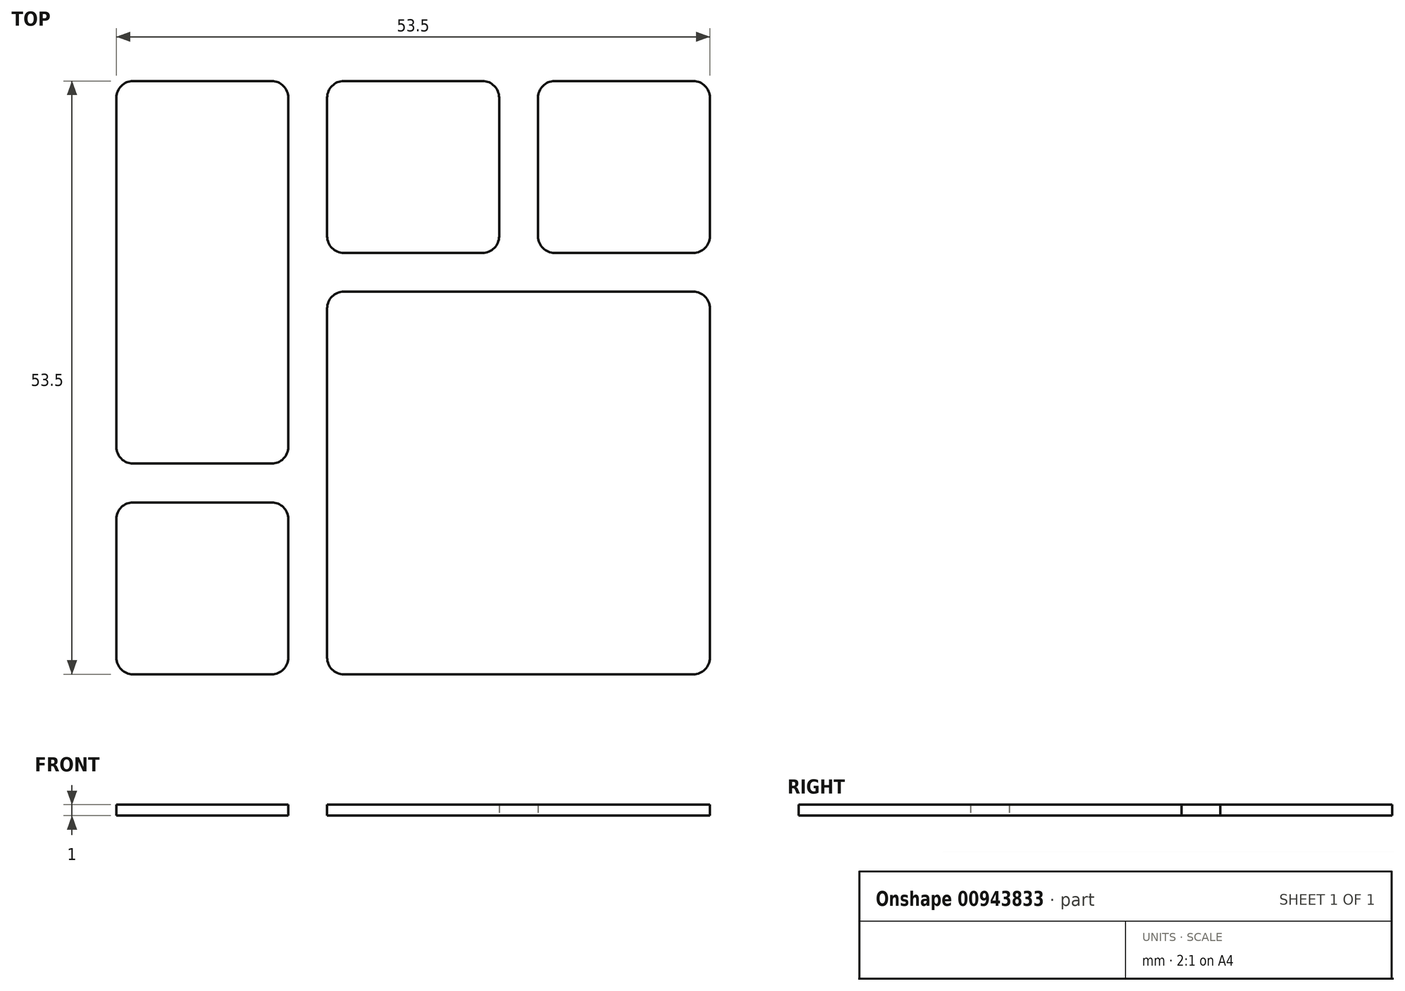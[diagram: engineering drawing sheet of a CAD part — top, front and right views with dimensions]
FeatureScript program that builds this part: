
annotation { "Feature Type Name" : "Feature", "Feature Type Description" : "" }
export const myFeature = defineFeature(function(context is Context, id is Id, definition is map)
    precondition{}
    {
        {
            var Q0;
            Q0=qCreatedBy(makeId("Top.planeOp"),FACE);
            var sketch = newSketch(context, id + "F0", { "sketchPlane" : qUnion([Q0])});
            skLineSegment(sketch, "E0.bottom", {"start": v(28.5, 28.5) * mm, "end": v(-28.5, 28.5) * mm, "construction": true});
            skLineSegment(sketch, "E0.top", {"start": v(28.5, -28.5) * mm, "end": v(-28.5, -28.5) * mm, "construction": true});
            skLineSegment(sketch, "E0.left", {"start": v(28.5, 28.5) * mm, "end": v(28.5, -28.5) * mm, "construction": true});
            skLineSegment(sketch, "E0.right", {"start": v(-28.5, 28.5) * mm, "end": v(-28.5, -28.5) * mm, "construction": true});
            skPoint(sketch, "E0.middle", {"position": v(0, 0) * mm});
            skLineSegment(sketch, "E1", {"start": v(-9.5, 28.5) * mm, "end": v(-9.5, -28.5) * mm, "construction": true});
            skLineSegment(sketch, "E2.1.0", {"start": v(-28.5, -9.5) * mm, "end": v(28.5, -9.5) * mm, "construction": true});
            skLineSegment(sketch, "E2.2.0", {"start": v(9.5, -28.5) * mm, "end": v(9.5, 28.5) * mm, "construction": true});
            skLineSegment(sketch, "E2.3.0", {"start": v(28.5, 9.5) * mm, "end": v(-28.5, 9.5) * mm, "construction": true});
            skLineSegment(sketch, "E3.bottom", {"start": v(-25.25, -11.25) * mm, "end": v(-12.75, -11.25) * mm});
            skLineSegment(sketch, "E3.top", {"start": v(-25.25, -26.75) * mm, "end": v(-12.75, -26.75) * mm});
            skLineSegment(sketch, "E3.left", {"start": v(-26.75, -12.75) * mm, "end": v(-26.75, -25.25) * mm});
            skLineSegment(sketch, "E3.right", {"start": v(-11.25, -12.75) * mm, "end": v(-11.25, -25.25) * mm});
            skLineSegment(sketch, "E4.top", {"start": v(-6.25, -26.75) * mm, "end": v(6.25, -26.75) * mm});
            skLineSegment(sketch, "E4.left", {"start": v(-7.75, -12.75) * mm, "end": v(-7.75, -25.25) * mm});
            skLineSegment(sketch, "E5.bottom", {"start": v(-6.25, 7.75) * mm, "end": v(6.25, 7.75) * mm});
            skLineSegment(sketch, "E5.left", {"start": v(-7.75, 6.25) * mm, "end": v(-7.75, -6.25) * mm});
            skPoint(sketch, "E6.visualSharp", {"position": v(-26.75, -11.25) * mm});
            skArc(sketch, "E6.filletArc", {"start": v(-25.25, -11.25) * mm, "mid": v(-26.31, -11.69) * mm, "end": v(-26.75, -12.75) * mm});
            skPoint(sketch, "E7.visualSharp", {"position": v(-11.25, -11.25) * mm});
            skArc(sketch, "E7.filletArc", {"start": v(-11.25, -12.75) * mm, "mid": v(-11.69, -11.69) * mm, "end": v(-12.75, -11.25) * mm});
            skPoint(sketch, "E8.visualSharp", {"position": v(-11.25, -26.75) * mm});
            skArc(sketch, "E8.filletArc", {"start": v(-12.75, -26.75) * mm, "mid": v(-11.69, -26.31) * mm, "end": v(-11.25, -25.25) * mm});
            skPoint(sketch, "E9.visualSharp", {"position": v(-26.75, -26.75) * mm});
            skArc(sketch, "E9.filletArc", {"start": v(-26.75, -25.25) * mm, "mid": v(-26.31, -26.31) * mm, "end": v(-25.25, -26.75) * mm});
            skPoint(sketch, "E10.visualSharp", {"position": v(-7.75, -26.75) * mm});
            skArc(sketch, "E10.filletArc", {"start": v(-7.75, -25.25) * mm, "mid": v(-7.31, -26.31) * mm, "end": v(-6.25, -26.75) * mm});
            skPoint(sketch, "E11.visualSharp", {"position": v(-7.75, 7.75) * mm});
            skArc(sketch, "E11.filletArc", {"start": v(-6.25, 7.75) * mm, "mid": v(-7.31, 7.31) * mm, "end": v(-7.75, 6.25) * mm});
            skLineSegment(sketch, "E12.1.2", {"start": v(26.75, -25.25) * mm, "end": v(26.75, -12.75) * mm});
            skLineSegment(sketch, "E12.1.6", {"start": v(12.75, 7.75) * mm, "end": v(25.25, 7.75) * mm});
            skPoint(sketch, "E12.1.7", {"position": v(26.75, -26.75) * mm});
            skPoint(sketch, "E12.1.12", {"position": v(26.75, 7.75) * mm});
            skLineSegment(sketch, "E12.1.13", {"start": v(12.75, -26.75) * mm, "end": v(25.25, -26.75) * mm});
            skLineSegment(sketch, "E12.1.14", {"start": v(26.75, -6.25) * mm, "end": v(26.75, 6.25) * mm});
            skArc(sketch, "E12.1.18", {"start": v(26.75, 6.25) * mm, "mid": v(26.31, 7.31) * mm, "end": v(25.25, 7.75) * mm});
            skArc(sketch, "E12.1.22", {"start": v(25.25, -26.75) * mm, "mid": v(26.31, -26.31) * mm, "end": v(26.75, -25.25) * mm});
            skPoint(sketch, "E12.2.0", {"position": v(11.25, 11.25) * mm});
            skPoint(sketch, "E12.2.1", {"position": v(7.75, 26.75) * mm});
            skLineSegment(sketch, "E12.2.2", {"start": v(25.25, 26.75) * mm, "end": v(12.75, 26.75) * mm});
            skLineSegment(sketch, "E12.2.3", {"start": v(25.25, 11.25) * mm, "end": v(12.75, 11.25) * mm});
            skPoint(sketch, "E12.2.4", {"position": v(7.75, 11.25) * mm});
            skPoint(sketch, "E12.2.5", {"position": v(11.25, 26.75) * mm});
            skLineSegment(sketch, "E12.2.6", {"start": v(-7.75, 12.75) * mm, "end": v(-7.75, 25.25) * mm});
            skPoint(sketch, "E12.2.7", {"position": v(26.75, 26.75) * mm});
            skPoint(sketch, "E12.2.8", {"position": v(-7.75, 11.25) * mm});
            skPoint(sketch, "E12.2.9", {"position": v(26.75, 11.25) * mm});
            skLineSegment(sketch, "E12.2.10", {"start": v(6.25, 11.25) * mm, "end": v(-6.25, 11.25) * mm});
            skLineSegment(sketch, "E12.2.11", {"start": v(11.25, 12.75) * mm, "end": v(11.25, 25.25) * mm});
            skPoint(sketch, "E12.2.12", {"position": v(-7.75, 26.75) * mm});
            skLineSegment(sketch, "E12.2.13", {"start": v(26.75, 12.75) * mm, "end": v(26.75, 25.25) * mm});
            skLineSegment(sketch, "E12.2.14", {"start": v(6.25, 26.75) * mm, "end": v(-6.25, 26.75) * mm});
            skLineSegment(sketch, "E12.2.15", {"start": v(7.75, 12.75) * mm, "end": v(7.75, 25.25) * mm});
            skArc(sketch, "E12.2.16", {"start": v(7.75, 25.25) * mm, "mid": v(7.31, 26.31) * mm, "end": v(6.25, 26.75) * mm});
            skArc(sketch, "E12.2.17", {"start": v(-7.75, 12.75) * mm, "mid": v(-7.31, 11.69) * mm, "end": v(-6.25, 11.25) * mm});
            skArc(sketch, "E12.2.18", {"start": v(-6.25, 26.75) * mm, "mid": v(-7.31, 26.31) * mm, "end": v(-7.75, 25.25) * mm});
            skArc(sketch, "E12.2.19", {"start": v(6.25, 11.25) * mm, "mid": v(7.31, 11.69) * mm, "end": v(7.75, 12.75) * mm});
            skArc(sketch, "E12.2.20", {"start": v(12.75, 26.75) * mm, "mid": v(11.69, 26.31) * mm, "end": v(11.25, 25.25) * mm});
            skArc(sketch, "E12.2.21", {"start": v(25.25, 11.25) * mm, "mid": v(26.31, 11.69) * mm, "end": v(26.75, 12.75) * mm});
            skArc(sketch, "E12.2.22", {"start": v(26.75, 25.25) * mm, "mid": v(26.31, 26.31) * mm, "end": v(25.25, 26.75) * mm});
            skArc(sketch, "E12.2.23", {"start": v(11.25, 12.75) * mm, "mid": v(11.69, 11.69) * mm, "end": v(12.75, 11.25) * mm});
            skLineSegment(sketch, "E12.3.2", {"start": v(-26.75, 25.25) * mm, "end": v(-26.75, 12.75) * mm});
            skLineSegment(sketch, "E12.3.3", {"start": v(-11.25, 25.25) * mm, "end": v(-11.25, 12.75) * mm});
            skLineSegment(sketch, "E12.3.6", {"start": v(-12.75, -7.75) * mm, "end": v(-25.25, -7.75) * mm});
            skPoint(sketch, "E12.3.7", {"position": v(-26.75, 26.75) * mm});
            skPoint(sketch, "E12.3.8", {"position": v(-11.25, -7.75) * mm});
            skPoint(sketch, "E12.3.9", {"position": v(-11.25, 26.75) * mm});
            skLineSegment(sketch, "E12.3.10", {"start": v(-11.25, 6.25) * mm, "end": v(-11.25, -6.25) * mm});
            skPoint(sketch, "E12.3.12", {"position": v(-26.75, -7.75) * mm});
            skLineSegment(sketch, "E12.3.13", {"start": v(-12.75, 26.75) * mm, "end": v(-25.25, 26.75) * mm});
            skLineSegment(sketch, "E12.3.14", {"start": v(-26.75, 6.25) * mm, "end": v(-26.75, -6.25) * mm});
            skArc(sketch, "E12.3.17", {"start": v(-12.75, -7.75) * mm, "mid": v(-11.69, -7.31) * mm, "end": v(-11.25, -6.25) * mm});
            skArc(sketch, "E12.3.18", {"start": v(-26.75, -6.25) * mm, "mid": v(-26.31, -7.31) * mm, "end": v(-25.25, -7.75) * mm});
            skArc(sketch, "E12.3.21", {"start": v(-11.25, 25.25) * mm, "mid": v(-11.69, 26.31) * mm, "end": v(-12.75, 26.75) * mm});
            skArc(sketch, "E12.3.22", {"start": v(-25.25, 26.75) * mm, "mid": v(-26.31, 26.31) * mm, "end": v(-26.75, 25.25) * mm});
            skLineSegment(sketch, "E13", {"start": v(26.75, -12.75) * mm, "end": v(26.75, -6.25) * mm});
            skLineSegment(sketch, "E14", {"start": v(6.25, 7.75) * mm, "end": v(12.75, 7.75) * mm});
            skLineSegment(sketch, "E15", {"start": v(-7.75, -6.25) * mm, "end": v(-7.75, -12.75) * mm});
            skLineSegment(sketch, "E16", {"start": v(6.25, -26.75) * mm, "end": v(12.75, -26.75) * mm});
            skLineSegment(sketch, "E17", {"start": v(-11.25, 6.25) * mm, "end": v(-11.25, 12.75) * mm});
            skLineSegment(sketch, "E18", {"start": v(-26.75, 6.25) * mm, "end": v(-26.75, 12.75) * mm});
            skSolve(sketch);
        }
        {
            var Q0;
            Q0=qSketchRegion(id+"F0",true);
            extrude(context, id + "F1", {"entities" : qUnion([Q0]), "depth" : 1 * mm, "offsetDistance" : 25 * mm});
        }
    });
